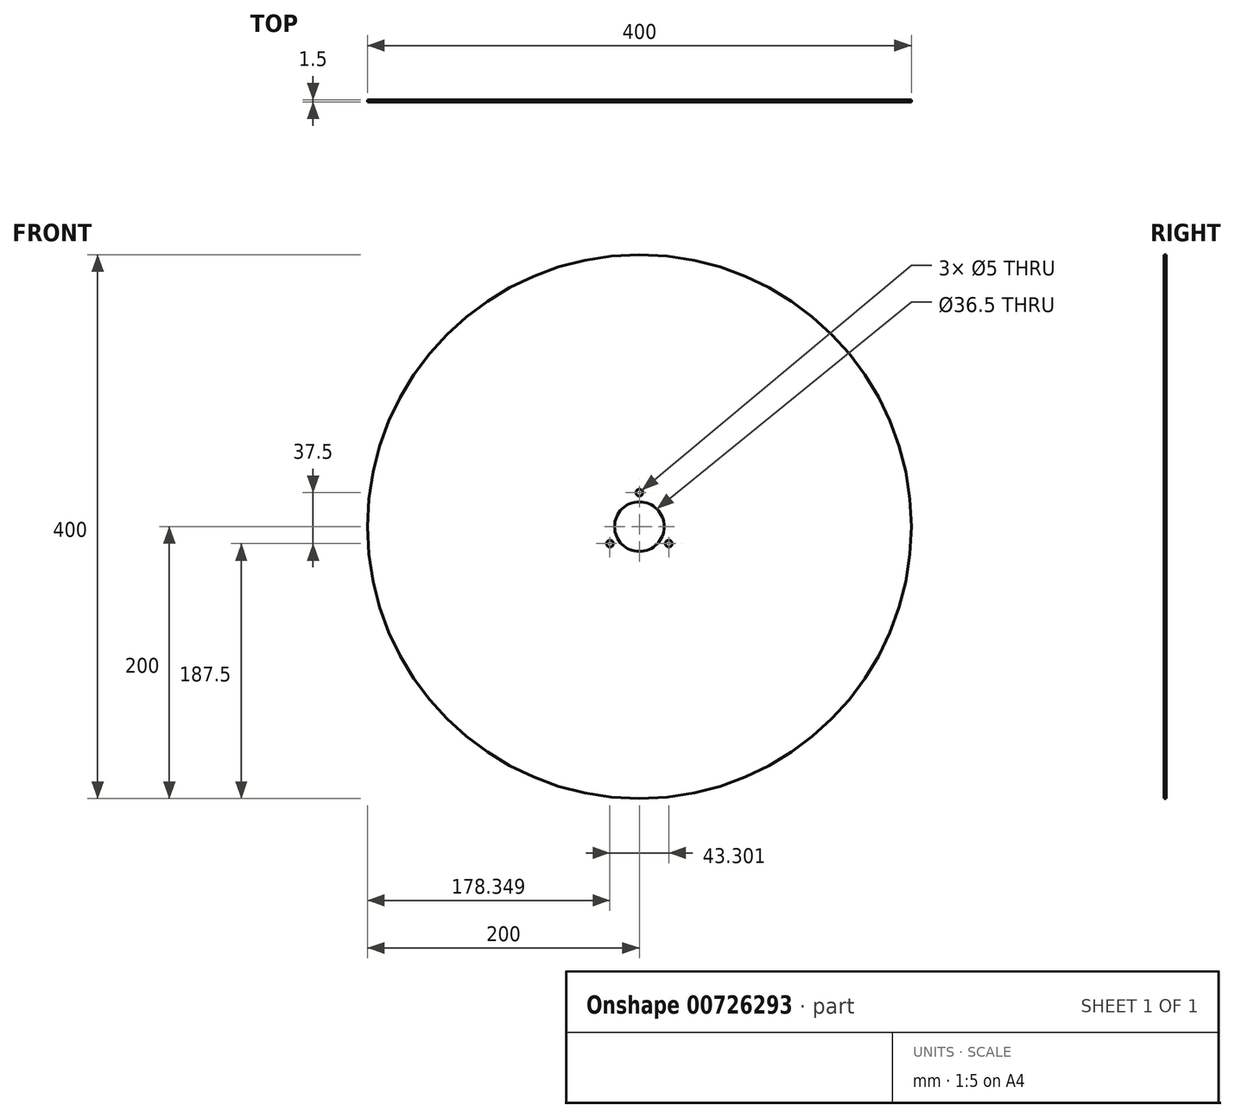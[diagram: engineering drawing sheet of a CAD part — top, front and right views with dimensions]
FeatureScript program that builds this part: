
annotation { "Feature Type Name" : "Feature", "Feature Type Description" : "" }
export const myFeature = defineFeature(function(context is Context, id is Id, definition is map)
    precondition{}
    {
        {
            var Q0;
            Q0=qCreatedBy(makeId("Front.planeOp"),FACE);
            var sketch = newSketch(context, id + "F0", { "sketchPlane" : qUnion([Q0])});
            skCircle(sketch, "E0", {"center": v(0, 0) * mm, "radius": 18.25 * mm});
            skCircle(sketch, "E1", {"center": v(0, 0) * mm, "radius": 200 * mm});
            skCircle(sketch, "E2", {"center": v(21.65, -12.5) * mm, "radius": 2.5 * mm});
            skCircle(sketch, "E3", {"center": v(0, 25) * mm, "radius": 2.5 * mm});
            skCircle(sketch, "E4", {"center": v(-21.65, -12.5) * mm, "radius": 2.5 * mm});
            skSolve(sketch);
        }
        {
            var Q0;
            Q0=makeQuery(id+"F0.imprint","IMPRINT",FACE,{"disambiguationData":[TD([[makeQuery(id+"F0.imprint","IMPRINT",EDGE,{"derivedFrom":sQuery(id+"F0.wireOp",EDGE,"E0")}),-1.0]])]});
            extrude(context, id + "F1", {"entities" : qUnion([Q0]), "depth" : 1.5 * mm, "offsetDistance" : 25 * mm});
        }
    });
